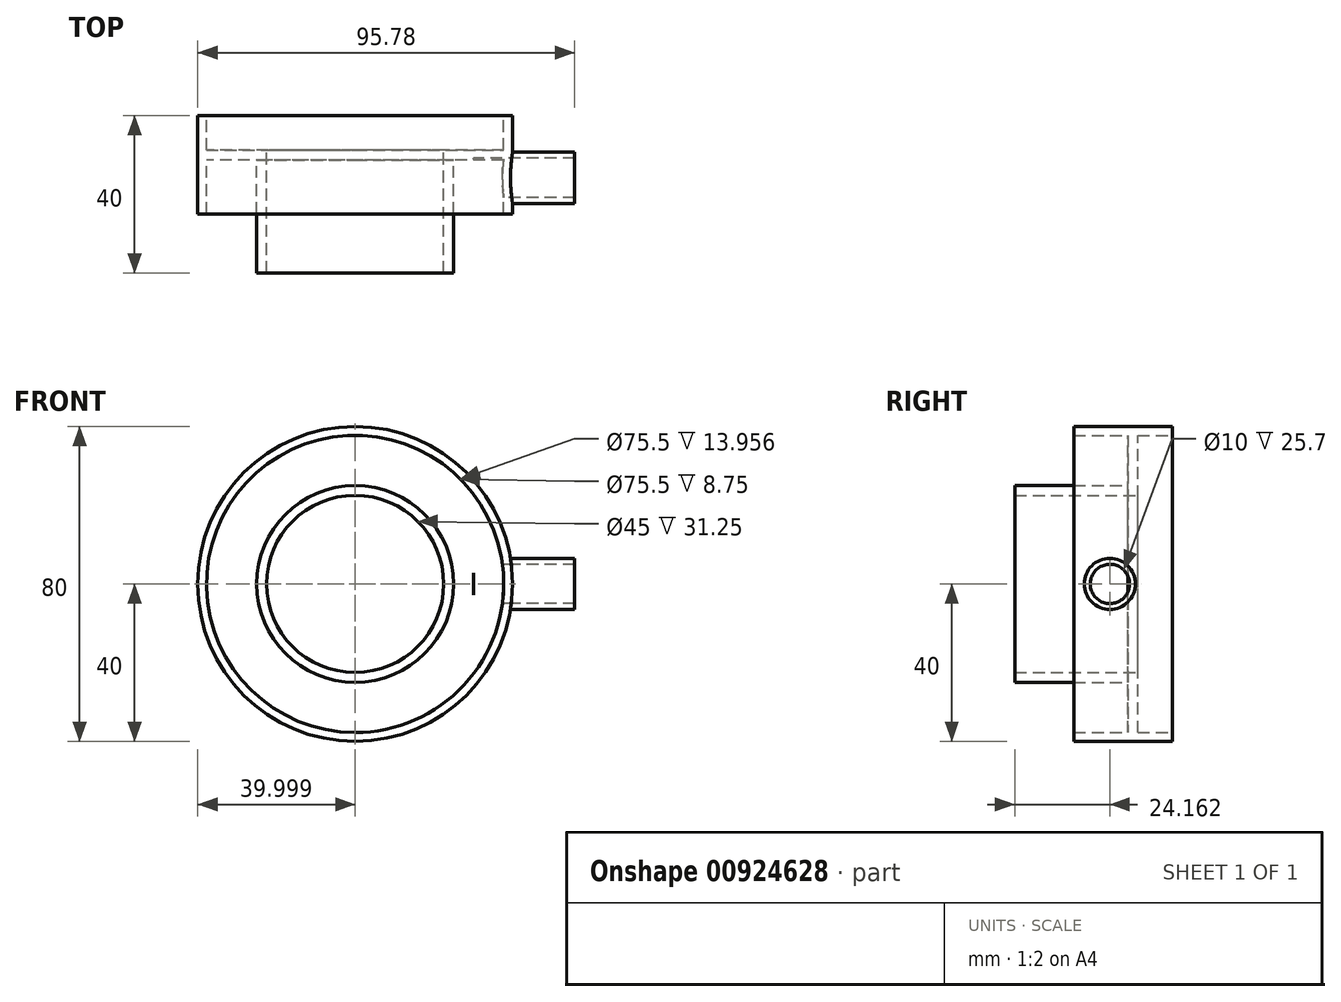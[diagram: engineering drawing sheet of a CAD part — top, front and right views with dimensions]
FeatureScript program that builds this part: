
annotation { "Feature Type Name" : "Feature", "Feature Type Description" : "" }
export const myFeature = defineFeature(function(context is Context, id is Id, definition is map)
    precondition{}
    {
        {
            var Q0;
            Q0=qCreatedBy(makeId("Front.planeOp"),FACE);
            var sketch = newSketch(context, id + "F0", { "sketchPlane" : qUnion([Q0])});
            skCircle(sketch, "E0", {"center": v(-137.48, 0) * mm, "radius": 37.75 * mm});
            skCircle(sketch, "E1", {"center": v(-137.48, 0) * mm, "radius": 40 * mm});
            skCircle(sketch, "E2", {"center": v(-137.48, 0) * mm, "radius": 25 * mm});
            skCircle(sketch, "E3", {"center": v(-137.48, 0) * mm, "radius": 22.5 * mm});
            skSolve(sketch);
        }
        {
            var Q0;
            Q0 = qSketchRegion(id + "F0", true);
            extrude(context, id + "F1", {"entities" : qUnion([Q0]), "depth" : 15 * mm, "offsetDistance" : 25 * mm});
        }
        {
            var Q0;
            Q0=makeQuery(id+"F1.opExtrude","CAP_FACE",FACE,{"disambiguationData":[OSD([sQuery(id+"F0.wireOp",EDGE,"E0"),sQuery(id+"F0.wireOp",EDGE,"E1")])],"isStart":true});
            extrude(context, id + "F2", {"entities" : qUnion([Q0]), "operationType" : NewBodyOperationType.ADD, "depth" : 10 * mm, "offsetDistance" : 25 * mm});
        }
        {
            var Q0;
            Q0=makeQuery(id+"F0.imprint","IMPRINT",FACE,{"disambiguationData":[TD([[makeQuery(id+"F0.imprint","IMPRINT",EDGE,{"derivedFrom":sQuery(id+"F0.wireOp",EDGE,"E0")}),1.0]])]});
            extrude(context, id + "F3", {"entities" : qUnion([Q0]), "operationType" : NewBodyOperationType.ADD, "depth" : 2.5 * mm, "offsetDistance" : 25 * mm, "symmetric" : true});
        }
        {
            var Q0;
            Q0=makeQuery(id+"F0.imprint","IMPRINT",FACE,{"disambiguationData":[TD([[makeQuery(id+"F0.imprint","IMPRINT",EDGE,{"derivedFrom":sQuery(id+"F0.wireOp",EDGE,"E2")}),1.0]])]});
            extrude(context, id + "F4", {"entities" : qUnion([Q0]), "operationType" : NewBodyOperationType.ADD, "depth" : 30 * mm, "offsetDistance" : 25 * mm});
        }
        {
            var Q0;
            Q0=makeQuery(id+"F4.opExtrude","CAP_FACE",FACE,{"disambiguationData":[OSD([sQuery(id+"F0.wireOp",EDGE,"E2"),sQuery(id+"F0.wireOp",EDGE,"E3")])],"isStart":true});
            extrude(context, id + "F5", {"entities" : qUnion([Q0]), "operationType" : NewBodyOperationType.ADD, "depth" : 1.25 * mm, "offsetDistance" : 25 * mm});
        }
        {
            var Q0;
            Q0=qCreatedBy(makeId("Right.planeOp"),FACE);
            cPlane(context, id + "F6", {"entities" : qUnion([Q0]), "cplaneType" : CPlaneType.OFFSET, "offset" : 107.4 * mm, "oppositeDirection" : true, "width" : 150 * mm, "height" : 150 * mm});
        }
        {
            var Q0;
            Q0=qCreatedBy(id+"F6.planeOp",FACE);
            var sketch = newSketch(context, id + "F7", { "sketchPlane" : qUnion([Q0])});
            skCircle(sketch, "E4", {"center": v(-5.84, 0) * mm, "radius": 5 * mm});
            skSolve(sketch);
        }
        {
            var Q0;
            Q0 = qSketchRegion(id + "F7", true);
            extrude(context, id + "F8", {"entities" : qUnion([Q0]), "operationType" : NewBodyOperationType.REMOVE, "depth" : 39 * mm, "offsetDistance" : 25 * mm});
        }
        {
            var Q0;
            Q0=makeQuery(id+"F8.boolean.opBoolean","INTERSECT",EDGE,{"disambiguationData":[OD(0.0)],"derivedFrom":[makeQuery(id+"F3.opExtrude","CAP_FACE",FACE,{"disambiguationData":[OSD([sQuery(id+"F0.wireOp",EDGE,"E0"),sQuery(id+"F0.wireOp",EDGE,"E2")])],"isStart":false}),makeQuery(id+"F8.opExtrude","SWEPT_FACE",FACE,{"disambiguationData":[OSD([sQuery(id+"F7.wireOp",EDGE,"E4")])]})]});
            var Q1;
            Q1=makeQuery(id+"F8.boolean.opBoolean","INTERSECT",EDGE,{"disambiguationData":[OD(1.0)],"derivedFrom":[makeQuery(id+"F3.opExtrude","CAP_FACE",FACE,{"disambiguationData":[OSD([sQuery(id+"F0.wireOp",EDGE,"E0"),sQuery(id+"F0.wireOp",EDGE,"E2")])],"isStart":false}),makeQuery(id+"F8.opExtrude","SWEPT_FACE",FACE,{"disambiguationData":[OSD([sQuery(id+"F7.wireOp",EDGE,"E4")])]})]});
            fillet(context, id + "F9", {"entities" : qUnion([Q0, Q1]), "radius" : 5 * mm, "tangentPropagation" : true, "allowEdgeOverflow" : false});
        }
        {
            var Q0;
            Q0=qCreatedBy(id+"F6.planeOp",FACE);
            cPlane(context, id + "F10", {"entities" : qUnion([Q0]), "cplaneType" : CPlaneType.OFFSET, "offset" : 8.7 * mm, "width" : 150 * mm, "height" : 150 * mm});
        }
        {
            var Q0;
            Q0=qCreatedBy(id+"F10.planeOp",FACE);
            var sketch = newSketch(context, id + "F11", { "sketchPlane" : qUnion([Q0])});
            skCircle(sketch, "E5", {"center": v(-5.84, 0) * mm, "radius": 6.5 * mm});
            skCircle(sketch, "E6", {"center": v(-5.84, 0) * mm, "radius": 5 * mm});
            skSolve(sketch);
        }
        {
            var Q0;
            Q0 = qSketchRegion(id + "F11", true);
            extrude(context, id + "F12", {"entities" : qUnion([Q0]), "operationType" : NewBodyOperationType.ADD, "depth" : 17 * mm, "offsetDistance" : 25 * mm});
        }
        {
            var Q0;
            Q0 = qSketchRegion(id + "F11", true);
            extrude(context, id + "F13", {"entities" : qUnion([Q0]), "operationType" : NewBodyOperationType.ADD, "depth" : 10 * mm, "offsetDistance" : 25 * mm});
        }
    });
